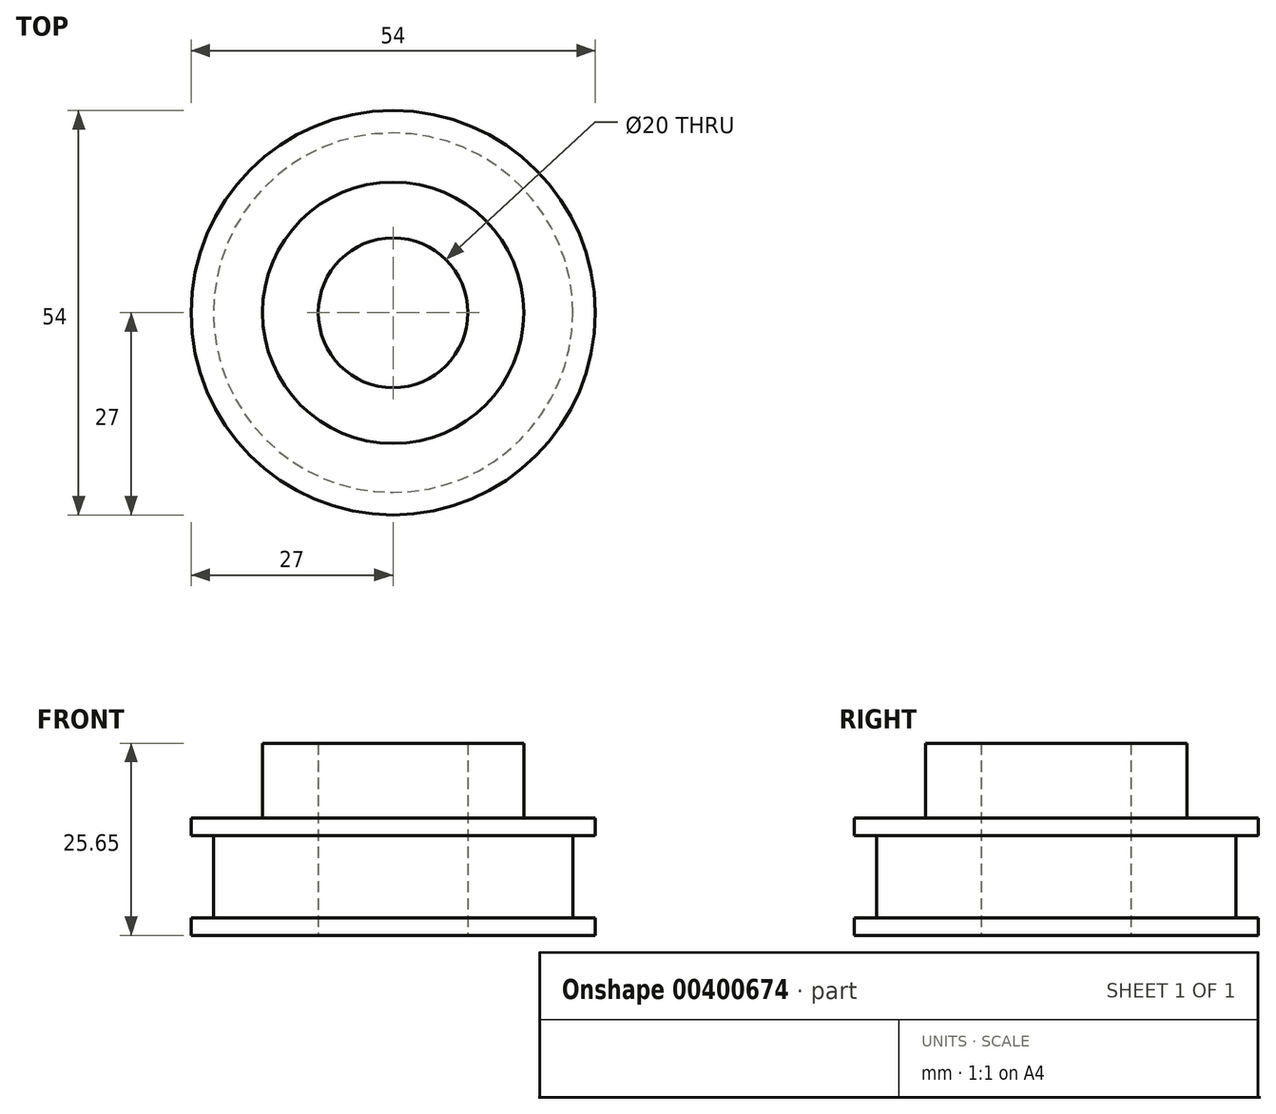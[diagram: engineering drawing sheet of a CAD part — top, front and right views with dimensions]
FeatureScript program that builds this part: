
annotation { "Feature Type Name" : "Feature", "Feature Type Description" : "" }
export const myFeature = defineFeature(function(context is Context, id is Id, definition is map)
    precondition{}
    {
        {
            var Q0;
            Q0=qCreatedBy(makeId("Front.planeOp"),FACE);
            var sketch = newSketch(context, id + "F0", { "sketchPlane" : qUnion([Q0])});
            skLineSegment(sketch, "E0.bottom", {"start": v(0, 0) * mm, "end": v(17, 0) * mm});
            skLineSegment(sketch, "E0.top", {"start": v(0, 15.7) * mm, "end": v(17, 15.7) * mm});
            skLineSegment(sketch, "E0.left", {"start": v(0, 0) * mm, "end": v(0, 2.35) * mm});
            skLineSegment(sketch, "E0.right", {"start": v(17, 0) * mm, "end": v(17, 15.7) * mm});
            skLineSegment(sketch, "E1", {"start": v(27, 0) * mm, "end": v(27, 15.7) * mm});
            skLineSegment(sketch, "E2", {"start": v(17, 15.7) * mm, "end": v(17, 25.65) * mm});
            skLineSegment(sketch, "E3", {"start": v(17, 25.65) * mm, "end": v(17, 15.7) * mm});
            skLineSegment(sketch, "E4", {"start": v(17, 15.7) * mm, "end": v(9.55, 15.7) * mm});
            skLineSegment(sketch, "E5", {"start": v(9.55, 15.7) * mm, "end": v(9.55, 25.65) * mm});
            skLineSegment(sketch, "E6", {"start": v(9.55, 25.65) * mm, "end": v(17, 25.65) * mm});
            skLineSegment(sketch, "E7", {"start": v(0, 15.7) * mm, "end": v(0, 13.35) * mm});
            skLineSegment(sketch, "E8", {"start": v(0, 2.35) * mm, "end": v(0, 0) * mm});
            skLineSegment(sketch, "E9", {"start": v(0, 2.35) * mm, "end": v(3, 2.35) * mm});
            skLineSegment(sketch, "E10", {"start": v(0, 13.35) * mm, "end": v(3, 13.35) * mm});
            skLineSegment(sketch, "E11", {"start": v(3, 13.35) * mm, "end": v(3, 2.35) * mm});
            skLineSegment(sketch, "E12.trimOffspring", {"start": v(0, 13.35) * mm, "end": v(0, 15.7) * mm});
            skSolve(sketch);
        }
        {
            var Q0;
            Q0 = qSketchRegion(id + "F0", true);
            var Q1;
            Q1 = qSketchRegion(id + "F2", true);
            var Q2;
            Q2=sQuery(id+"F0.wireOp",EDGE,"E1");
            revolve(context, id + "F1", {"entities" : qUnion([Q0, Q1]), "axis" : qUnion([Q2]), "revolveType" : RevolveType.FULL});
        }
    });
